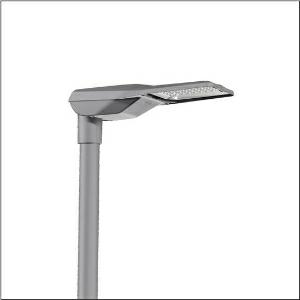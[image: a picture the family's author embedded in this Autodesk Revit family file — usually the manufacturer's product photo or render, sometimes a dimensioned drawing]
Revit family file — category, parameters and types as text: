
# Revit family: streetlight_sl_21_iq_mini___p0_8a_5xe2u31g08jb_9ae4
name_source: partatom
category: Lighting Fixtures
units: mm (PartAtom-declared; Revit-internal decimal feet)

## family parameters
Cut with Voids When Loaded = No
Host = Face
Light Source = No
Part Type = Normal
Room Calculation Point = No
Round Connector Dimension = Use Diameter
Shared = No

## types (1)
- --- (1 x LED, 10920 lm, 71.6 W, 3000K)
    Apparent Load = 72 VA
    CIE Flux Codes = 36 69 97 100 100
    Color Rendering = 70
    Color Temperature = 3000K
    Default Elevation = 1800 mm
    Description = Streetlight SL 21 iQ mini, mast luminaire, primary light control with lens, of PMMA, primary optical cover: cover, of toughened safety glass, transparent, light distribution: P0.8a, light emission: direct distribution, primary light characteristic: asymmetric, installation type: post-top, side-entry, LED, High Power LED, rated luminous flux: 10.920lm, luminous efficacy: 153lm/W, light colour: 730, colour temperature: 3000K, control gear: iQ Street-Remote, control: pre-setting: linear dimming characteristic, Street-Remote, Auto-Match, Temp-Guard, Lumen-Switch, Night-Set, Smart-Wire, Light-Fading, Desk-Remote (wireless, voltage-free reading and setting of iQ features in the workshop via application-optimized NFC function/RFID function), optimised constant luminous flux control (CLO 2.0), mains connection: 220..240V, AC, 50/60Hz, start of lifetime: 72W, end of service life: 75W, reduction: 33W, luminaire housing, of diecast aluminium, powder-coated, SITECO metallic grey (DB 702S), corrosivity category C5 high according to DIN EN ISO 12944, please order mast flange separately, inclination adjustable: 0°, 5°, 10°, 15°, sealing non-destructively replaceable, multi-level sealing system, length: 628mm, width: 235mm, height: 110mm, mast flange for spigot size: 42mm (side-entry): 5XC10008XM4, 60/48mm (side-entry/post-top): 5XC10108XM2, 76/60mm (side-entry/post-top): 5XC10108XM1, mounting height: 4..8m, protection rating (complete): IP66, insulation class (complete): insulation class II (safety insulation), certification: CE, ENEC, ENEC+, VDE, impact resistance: IK10, permissible operating ambient temperature for outdoor applications: -40..+50°C, standard-compliant lighting for roads and squares, packaging unit: 1 piece

Light Distribution: P0.8a
    Height = 110 mm
    Lamp = 1 x LED
    Lamp Light Flux = 10920 lm
    Lamp Power = 71.6 W
    Lamp count = 1
    Length = 625 mm
    Luminous efficacy = 153 lm/W
    Manufacturer = Siteco
    ModVariant = No
    Model = 5XE2U31G08JB
    Number of Poles = 1
    OnlyDefault = Yes
    Power Factor = 1
    Product Name = Streetlight SL 21 iQ mini | P0.8a
    Product group = mast luminaire | pylon top
    ProductGroupID = 6100
    Protection Class = Protection class II
    Protection Degree = IP 66
    RLX_Detail_Level = 1
    RLX_Emergency_Light_Flux = 0 lm
    RLX_Emergency_Type = 0
    RLX_Emergency_Type_DB = No
    RlxData = <blob elided: 92265 chars, md5=307bcfe4>
    Socket = socket
    Standby Power = 0 W
    System Light Flux = 10920 lm
    System Power = 72 W
    Type Comments = factory setting: luminous flux: 100 % | dim-lin: 254 | 746 mA
    Type Image = l_1003519.jpg
    URL = http://relux.com
    VarID = @adj_079337
    Voltage = 0 V
    Weight = 0.00 kg
    Width = 234 mm

## geometry (parser evidence)
native form markers: Blend x4, Sweep x11
no freeform markers — native parametric forms only
